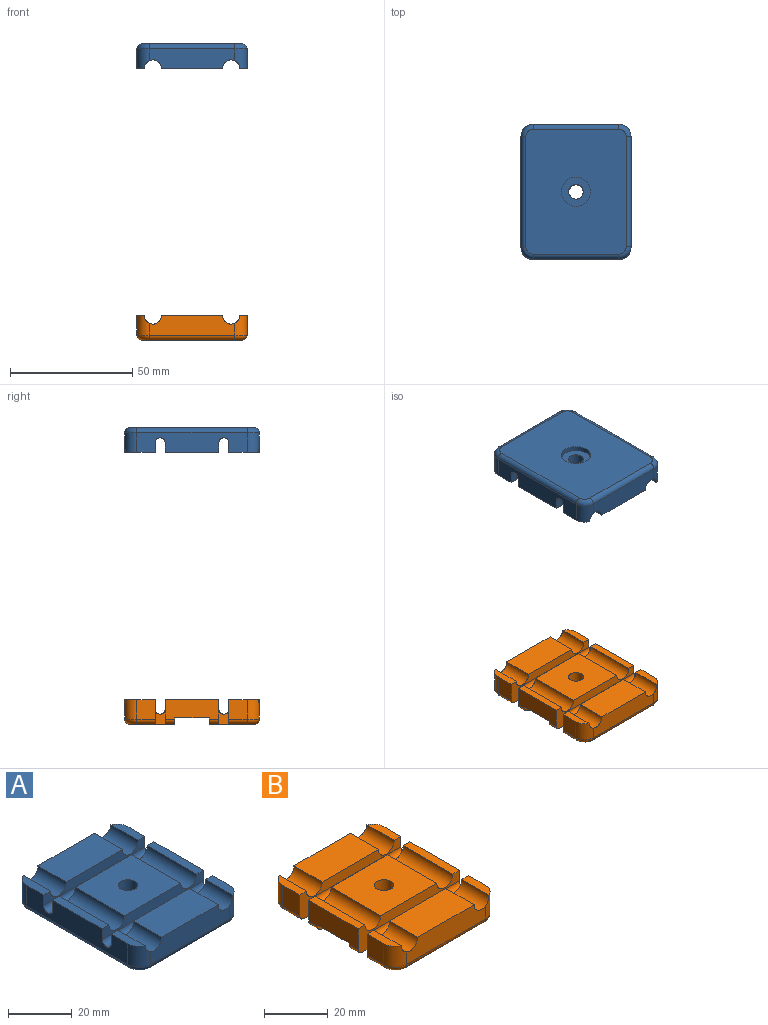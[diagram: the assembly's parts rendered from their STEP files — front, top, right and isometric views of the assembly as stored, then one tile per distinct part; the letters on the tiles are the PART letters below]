
ASSEMBLY  parts=2 mates=1
PART A: 41 faces, bbox 45.8x55.8x10 mm
  f0: plane 25x22mm, normal (0,0,1), area 521.7mm2, adj f6,f8,f10,f35,f38
  f1: plane 25x12.5mm, normal (0,0,1), area 312.5mm2, adj f7,f9,f14,f36
  f2: plane 22x3mm, normal (0,0,1), area 66mm2, adj f6,f16,f35,f38
  f3: plane 12.08x3mm, normal (0,0,1), area 32.4mm2, adj f7,f16,f24,f36
  f4: plane 22x3mm, normal (0,0,1), area 66mm2, adj f8,f15,f35,f38
  f5: plane 12.08x3mm, normal (0,0,1), area 32.4mm2, adj f9,f15,f21,f36
  f6: cylinder r=3.5mm len=22mm, axis (0,-1,0), area 241.9mm2, adj f0,f2,f35,f38
  f7: cylinder r=3.5mm len=12.5mm, axis (0,-1,0), area 136.6mm2, adj f1,f3,f14,f24,f36
  f8: cylinder r=3.5mm len=22mm, axis (0,-1,0), area 241.9mm2, adj f0,f4,f35,f38
  f9: cylinder r=3.5mm len=12.5mm, axis (0,-1,0), area 136.6mm2, adj f1,f5,f14,f21,f36
  f10: cylinder r=3mm len=8mm, axis (0,0,-1), area 150.8mm2, adj f0,f34
  f11: plane 25x12.5mm, normal (0,0,1), area 312.5mm2, adj f13,f19,f20,f37
  f12: plane 12.08x3mm, normal (0,0,1), area 32.4mm2, adj f16,f19,f23,f37
  f13: plane 35x8mm, normal (0,-1,0), area 250.6mm2, adj f11,f19,f20,f22,f23,f25
  f14: plane 35x8mm, normal (0,1,0), area 250.6mm2, adj f1,f7,f9,f21,f24,f32
  f15: plane 45x8mm, normal (-1,0,0), area 315.4mm2, adj f4,f5,f17,f21,f22,f28,f35,f36
  f16: plane 45x8mm, normal (1,0,0), area 315.4mm2, adj f2,f3,f12,f23,f24,f29,f35,f36
  f17: plane 12.08x3mm, normal (0,0,1), area 32.4mm2, adj f15,f20,f22,f37
  f18: plane 51x41mm, normal (0,0,-1), area 1970.2mm2, adj f25,f26,f27,f28,f29,f30,f31,f32
  f19: cylinder r=3.5mm len=12.5mm, axis (0,-1,0), area 136.6mm2, adj f11,f12,f13,f23,f37
  f20: cylinder r=3.5mm len=12.5mm, axis (0,-1,0), area 136.6mm2, adj f11,f13,f17,f22,f37
  f21: cylinder r=5mm len=8mm, axis (0,0,1), area 58.2mm2, adj f5,f9,f14,f15,f30
  f22: cylinder r=5mm len=8mm, axis (0,0,-1), area 58.2mm2, adj f13,f15,f17,f20,f26
  f23: cylinder r=5mm len=8mm, axis (0,0,1), area 58.2mm2, adj f12,f13,f16,f19,f27
  f24: cylinder r=5mm len=8mm, axis (0,0,-1), area 58.2mm2, adj f3,f7,f14,f16,f31
  f25: cylinder r=2mm len=35mm, axis (1,0,0), area 110mm2, adj f13,f18,f26,f27
  f26: torus R=3mm, axis (0,0,1), area 21.1mm2, adj f18,f22,f25,f28
  f27: torus R=3mm, axis (0,0,1), area 21.1mm2, adj f18,f23,f25,f29
  f28: cylinder r=2mm len=45mm, axis (0,-1,0), area 141.4mm2, adj f15,f18,f26,f30
  f29: cylinder r=2mm len=45mm, axis (0,1,0), area 141.4mm2, adj f16,f18,f27,f31
  f30: torus R=3mm, axis (0,0,1), area 21.1mm2, adj f18,f21,f28,f32
  f31: torus R=3mm, axis (0,0,1), area 21.1mm2, adj f18,f24,f29,f32
  f32: cylinder r=2mm len=35mm, axis (-1,0,0), area 110mm2, adj f14,f18,f30,f31
  f33: cylinder r=6mm len=12mm, axis (0,0,-1), area 75.4mm2, adj f18,f34
  f34: plane 12x12mm, normal (0,0,-1), area 84.8mm2, adj f10,f33
  f35: plane 45x4mm, normal (0,1,0), area 141.5mm2, adj f0,f2,f4,f6,f8,f15,f16,f39
  f36: plane 45x4mm, normal (0,-1,0), area 141.5mm2, adj f1,f3,f5,f7,f9,f15,f16,f39
  f37: plane 45x4mm, normal (0,1,0), area 141.5mm2, adj f11,f12,f15,f16,f17,f19,f20,f40
  f38: plane 45x4mm, normal (0,-1,0), area 141.5mm2, adj f0,f2,f4,f6,f8,f15,f16,f40
  f39: cylinder r=2mm len=45mm, axis (1,0,0), area 282.7mm2, adj f15,f16,f35,f36
  f40: cylinder r=2mm len=45mm, axis (1,0,0), area 282.7mm2, adj f15,f16,f37,f38
PART B: 51 faces, bbox 45.8x55.8x10 mm
  f0: plane 8x7.5mm, normal (-1,0,0), area 60mm2, adj f22,f29,f42,f48
  f1: plane 22x8mm, normal (-1,0,0), area 169mm2, adj f4,f9,f24,f25,f26,f37,f38,f41
  f2: plane 41x18.5mm, normal (0,0,-1), area 742.6mm2, adj f3,f26,f33,f34,f35,f36,f37,f38
  f3: cylinder r=2mm len=7.5mm, axis (0,-1,0), area 23.6mm2, adj f2,f11,f36,f39
  f4: cylinder r=2mm len=4mm, axis (0,-1,0), area 12.6mm2, adj f1,f23,f25,f41
  f5: plane 25x22mm, normal (0,0,1), area 521.7mm2, adj f13,f15,f20,f38,f41
  f6: plane 25x12.5mm, normal (0,0,1), area 312.5mm2, adj f14,f16,f19,f39
  f7: plane 22x3mm, normal (0,0,1), area 66mm2, adj f12,f13,f38,f41
  f8: plane 12.08x3mm, normal (0,0,1), area 32.4mm2, adj f12,f14,f31,f39
  f9: plane 22x3mm, normal (0,0,1), area 66mm2, adj f1,f15,f38,f41
  f10: plane 12.08x3mm, normal (0,0,1), area 32.4mm2, adj f11,f16,f30,f39
  f11: plane 8x7.5mm, normal (-1,0,0), area 60mm2, adj f3,f10,f30,f39
  f12: plane 45x8mm, normal (1,0,0), area 308.4mm2, adj f7,f8,f18,f24,f25,f26,f31,f32
  f13: cylinder r=3.5mm len=22mm, axis (0,-1,0), area 241.9mm2, adj f5,f7,f38,f41
  f14: cylinder r=3.5mm len=12.5mm, axis (0,-1,0), area 136.6mm2, adj f6,f8,f19,f31,f39
  f15: cylinder r=3.5mm len=22mm, axis (0,-1,0), area 241.9mm2, adj f5,f9,f38,f41
  f16: cylinder r=3.5mm len=12.5mm, axis (0,-1,0), area 136.6mm2, adj f6,f10,f19,f30,f39
  f17: plane 25x12.5mm, normal (0,0,1), area 312.5mm2, adj f21,f27,f28,f42
  f18: plane 12.08x3mm, normal (0,0,1), area 32.4mm2, adj f12,f27,f32,f42
  f19: plane 35x8mm, normal (0,-1,0), area 250.6mm2, adj f6,f14,f16,f30,f31,f35
  f20: cylinder r=3mm len=7.5mm, axis (0,0,-1), area 141.4mm2, adj f5,f24
  f21: plane 35x8mm, normal (0,1,0), area 250.6mm2, adj f17,f27,f28,f29,f32,f46
  f22: plane 12.08x3mm, normal (0,0,1), area 32.4mm2, adj f0,f28,f29,f42
  f23: plane 41x18.5mm, normal (0,0,-1), area 742.6mm2, adj f4,f25,f41,f42,f44,f45,f46,f47
  f24: plane 45x14mm, normal (0,0,-1), area 601.7mm2, adj f1,f12,f20,f25,f26
  f25: plane 45x2.5mm, normal (0,-1,0), area 110.8mm2, adj f1,f4,f12,f23,f24,f44
  f26: plane 45x2.5mm, normal (0,1,0), area 110.8mm2, adj f1,f2,f12,f24,f33,f37
  f27: cylinder r=3.5mm len=12.5mm, axis (0,-1,0), area 136.6mm2, adj f17,f18,f21,f32,f42
  f28: cylinder r=3.5mm len=12.5mm, axis (0,-1,0), area 136.6mm2, adj f17,f21,f22,f29,f42
  f29: cylinder r=5mm len=8mm, axis (0,0,1), area 58.2mm2, adj f0,f21,f22,f28,f47
  f30: cylinder r=5mm len=8mm, axis (0,0,-1), area 58.2mm2, adj f10,f11,f16,f19,f36
  f31: cylinder r=5mm len=8mm, axis (0,0,1), area 58.2mm2, adj f8,f12,f14,f19,f34
  f32: cylinder r=5mm len=8mm, axis (0,0,-1), area 58.2mm2, adj f12,f18,f21,f27,f45
  f33: cylinder r=2mm len=15.5mm, axis (0,1,0), area 48.7mm2, adj f2,f12,f26,f34
  f34: torus R=3mm, axis (0,0,1), area 21.1mm2, adj f2,f31,f33,f35
  f35: cylinder r=2mm len=35mm, axis (1,0,0), area 110mm2, adj f2,f19,f34,f36
  f36: torus R=3mm, axis (0,0,1), area 21.1mm2, adj f2,f3,f30,f35
  f37: cylinder r=2mm len=4mm, axis (0,-1,0), area 12.6mm2, adj f1,f2,f26,f38
  f38: plane 45x10mm, normal (0,-1,0), area 170.7mm2, adj f1,f2,f5,f7,f9,f12,f13,f15
  f39: plane 45x10mm, normal (0,1,0), area 170.7mm2, adj f2,f3,f6,f8,f10,f11,f12,f14
  f40: cylinder r=2mm len=40mm, axis (-1,0,0), area 251.3mm2, adj f12,f38,f39,f50
  f41: plane 45x10mm, normal (0,1,0), area 170.7mm2, adj f1,f4,f5,f7,f9,f12,f13,f15
  f42: plane 45x10mm, normal (0,-1,0), area 170.7mm2, adj f0,f12,f17,f18,f22,f23,f27,f28
  f43: cylinder r=2mm len=40mm, axis (-1,0,0), area 251.3mm2, adj f12,f41,f42,f49
  f44: cylinder r=2mm len=15.5mm, axis (0,1,0), area 48.7mm2, adj f12,f23,f25,f45
  f45: torus R=3mm, axis (0,0,1), area 21.1mm2, adj f23,f32,f44,f46
  f46: cylinder r=2mm len=35mm, axis (-1,0,0), area 110mm2, adj f21,f23,f45,f47
  f47: torus R=3mm, axis (0,0,1), area 21.1mm2, adj f23,f29,f46,f48
  f48: cylinder r=2mm len=7.5mm, axis (0,-1,0), area 23.6mm2, adj f0,f23,f42,f47
  f49: plane 6x4mm, normal (-1,0,0), area 17.7mm2, adj f23,f41,f42,f43
  f50: plane 6x4mm, normal (-1,0,0), area 17.7mm2, adj f2,f38,f39,f40
PLACE A rot(axis=(-1,0,0),180deg) t=(-14.61,132.32,123.22)mm
PLACE B rot(axis=(0.53,0.71,0.46),0deg) t=(-14.61,66.31,2.25)mm fixed
MATE slider A.f10 <-> B.f20  axis (0,0,-1) through (-46.81,99.31,113.22)mm
